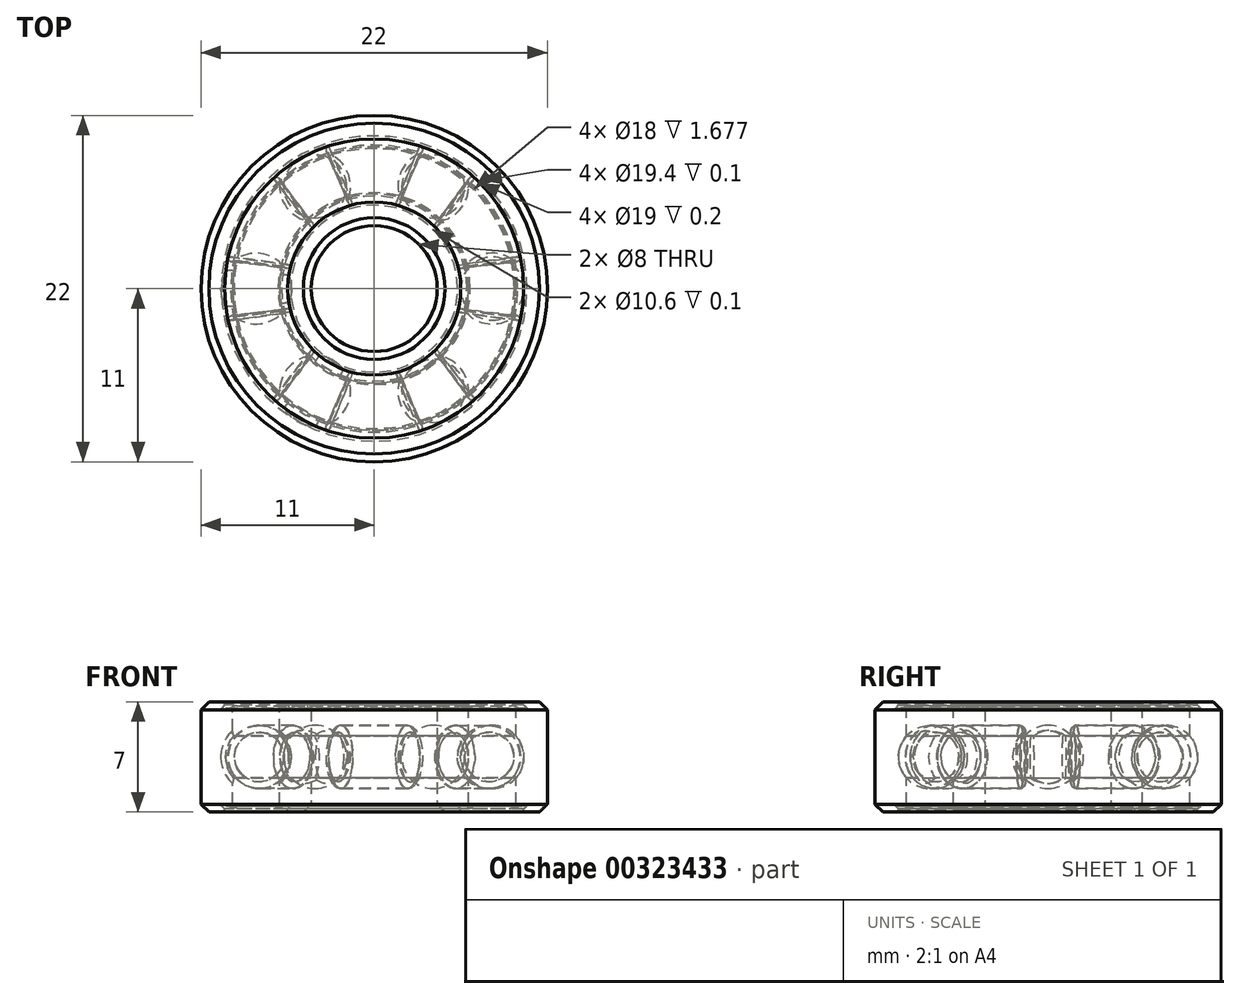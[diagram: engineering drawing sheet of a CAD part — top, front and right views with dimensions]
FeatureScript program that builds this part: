
annotation { "Feature Type Name" : "Feature", "Feature Type Description" : "" }
export const myFeature = defineFeature(function(context is Context, id is Id, definition is map)
    precondition{}
    {
        {
            var Q0;
            Q0=qCreatedBy(makeId("Top.planeOp"),FACE);
            var sketch = newSketch(context, id + "F0", { "sketchPlane" : qUnion([Q0])});
            skCircle(sketch, "E0", {"center": v(0, 0) * mm, "radius": 11 * mm});
            skCircle(sketch, "E1", {"center": v(0, 0) * mm, "radius": 4 * mm});
            skSolve(sketch);
        }
        {
            var Q0;
            Q0=makeQuery(id+"F0.imprint","IMPRINT",FACE,{"disambiguationData":[TD([[makeQuery(id+"F0.imprint","IMPRINT",EDGE,{"derivedFrom":sQuery(id+"F0.wireOp",EDGE,"E0")}),1.0]])]});
            extrude(context, id + "F1", {"entities" : qUnion([Q0]), "depth" : 7 * mm});
        }
        {
            var Q0;
            Q0=makeQuery(id+"F1.opExtrude","CAP_EDGE",EDGE,{"disambiguationData":[OSD([sQuery(id+"F0.wireOp",EDGE,"E0")])],"isStart":false});
            var Q1;
            Q1=makeQuery(id+"F1.opExtrude","CAP_EDGE",EDGE,{"disambiguationData":[OSD([sQuery(id+"F0.wireOp",EDGE,"E0")])],"isStart":true});
            var Q2;
            Q2=makeQuery(id+"F1.opExtrude","SWEPT_FACE",FACE,{"disambiguationData":[OSD([sQuery(id+"F0.wireOp",EDGE,"E1")])]});
            chamfer(context, id + "F2", {"entities" : qUnion([Q0, Q1, Q2]), "width" : .5 * mm, "tangentPropagation" : true});
        }
        {
            var Q0;
            Q0=qCreatedBy(makeId("Front.planeOp"),FACE);
            var sketch = newSketch(context, id + "F3", { "sketchPlane" : qUnion([Q0])});
            skCircle(sketch, "E2", {"center": v(-7.5, 3.5) * mm, "radius": 2 * mm});
            skLineSegment(sketch, "E3.0", {"start": v(-10.5, 7) * mm, "end": v(10.5, 7) * mm, "construction": true});
            skLineSegment(sketch, "E4.0", {"start": v(10.5, 0) * mm, "end": v(-10.5, 0) * mm, "construction": true});
            skLineSegment(sketch, "E5", {"start": v(-7.5, 3.5) * mm, "end": v(-7.5, 7) * mm, "construction": true});
            skLineSegment(sketch, "E6", {"start": v(-7.5, 3.5) * mm, "end": v(-7.5, 0) * mm, "construction": true});
            skLineSegment(sketch, "E7", {"start": v(0, 0) * mm, "end": v(0, 10.43) * mm, "construction": true});
            skLineSegment(sketch, "E8", {"start": v(-4, 0) * mm, "end": v(-4, 7) * mm, "construction": true});
            skLineSegment(sketch, "E9", {"start": v(-11, 0.5) * mm, "end": v(-11, 6.5) * mm});
            skLineSegment(sketch, "E10", {"start": v(-11, 6.5) * mm, "end": v(-10.5, 7) * mm});
            skLineSegment(sketch, "E11", {"start": v(-10.5, 0) * mm, "end": v(-11.25, 0.75) * mm});
            skLineSegment(sketch, "E12", {"start": v(-7.5, 3.5) * mm, "end": v(-11, 3.5) * mm, "construction": true});
            skLineSegment(sketch, "E13", {"start": v(-7.5, 3.5) * mm, "end": v(-4, 3.5) * mm, "construction": true});
            skLineSegment(sketch, "E14", {"start": v(-7.5, 5.5) * mm, "end": v(-7.5, 1.5) * mm});
            skLineSegment(sketch, "E15", {"start": v(-6, 4.82) * mm, "end": v(-6, 7) * mm, "construction": true});
            skLineSegment(sketch, "E16", {"start": v(-6, 7) * mm, "end": v(-9, 7) * mm});
            skLineSegment(sketch, "E17", {"start": v(-9, 7) * mm, "end": v(-9, 4.82) * mm});
            skLineSegment(sketch, "E18", {"start": v(-9, 2.18) * mm, "end": v(-9, 0) * mm});
            skLineSegment(sketch, "E19", {"start": v(-9, 0) * mm, "end": v(-6, 0) * mm});
            skLineSegment(sketch, "E20", {"start": v(-6, 0) * mm, "end": v(-6, 2.18) * mm, "construction": true});
            skLineSegment(sketch, "E21", {"start": v(-6, 6.5) * mm, "end": v(-5.5, 6.5) * mm});
            skLineSegment(sketch, "E22", {"start": v(-5.5, 6.8) * mm, "end": v(-5.5, 7) * mm});
            skLineSegment(sketch, "E23", {"start": v(-6, 0.5) * mm, "end": v(-5.5, 0.5) * mm});
            skLineSegment(sketch, "E24", {"start": v(-5.5, 0.2) * mm, "end": v(-5.5, 0) * mm});
            skLineSegment(sketch, "E25", {"start": v(-6, 2.18) * mm, "end": v(-6, 0.5) * mm});
            skLineSegment(sketch, "E26", {"start": v(-6, 4.82) * mm, "end": v(-6, 6.5) * mm});
            skLineSegment(sketch, "E27", {"start": v(-5.5, 7) * mm, "end": v(-9, 7) * mm});
            skLineSegment(sketch, "E28", {"start": v(-5.5, 0) * mm, "end": v(-9, 0) * mm});
            skLineSegment(sketch, "E29", {"start": v(-5.5, 6.8) * mm, "end": v(-5.3, 6.6) * mm});
            skLineSegment(sketch, "E30", {"start": v(-5.3, 6.6) * mm, "end": v(-5.3, 6.5) * mm});
            skLineSegment(sketch, "E31", {"start": v(-5.3, 6.5) * mm, "end": v(-5.5, 6.5) * mm});
            skLineSegment(sketch, "E32", {"start": v(-5.5, 6.8) * mm, "end": v(-5.5, 6.5) * mm, "construction": true});
            skLineSegment(sketch, "E33.MirrorCS", {"start": v(-9, 6.5) * mm, "end": v(-9.5, 6.5) * mm});
            skLineSegment(sketch, "E34.MirrorCS", {"start": v(-9.7, 6.5) * mm, "end": v(-9.5, 6.5) * mm});
            skLineSegment(sketch, "E35.MirrorCS", {"start": v(-9.7, 6.6) * mm, "end": v(-9.7, 6.5) * mm});
            skLineSegment(sketch, "E36.MirrorCS", {"start": v(-9.5, 6.8) * mm, "end": v(-9.7, 6.6) * mm});
            skLineSegment(sketch, "E37.MirrorCS", {"start": v(-9.5, 6.8) * mm, "end": v(-9.5, 7) * mm});
            skLineSegment(sketch, "E38", {"start": v(-9.5, 7) * mm, "end": v(-9, 7) * mm});
            skLineSegment(sketch, "E39.MirrorCS", {"start": v(-5.3, 0.5) * mm, "end": v(-5.5, 0.5) * mm});
            skLineSegment(sketch, "E40.MirrorCS", {"start": v(-5.3, 0.4) * mm, "end": v(-5.3, 0.5) * mm});
            skLineSegment(sketch, "E41.MirrorCS", {"start": v(-5.5, 0.2) * mm, "end": v(-5.3, 0.4) * mm});
            skLineSegment(sketch, "E42.MirrorCS", {"start": v(-9, 0.5) * mm, "end": v(-9.5, 0.5) * mm});
            skLineSegment(sketch, "E43.MirrorCS", {"start": v(-9.7, 0.5) * mm, "end": v(-9.5, 0.5) * mm});
            skLineSegment(sketch, "E44.MirrorCS", {"start": v(-9.5, 0.2) * mm, "end": v(-9.7, 0.4) * mm});
            skLineSegment(sketch, "E45.MirrorCS", {"start": v(-9.5, 0.2) * mm, "end": v(-9.5, 0) * mm});
            skLineSegment(sketch, "E46.MirrorCS", {"start": v(-9.7, 0.4) * mm, "end": v(-9.7, 0.5) * mm});
            skLineSegment(sketch, "E47", {"start": v(-5.5, 0.2) * mm, "end": v(-5.5, 0.5) * mm, "construction": true});
            skLineSegment(sketch, "E48", {"start": v(-9, 0) * mm, "end": v(-9.5, 0) * mm});
            skSolve(sketch);
        }
        {
            var Q0;
            Q0 = qSketchRegion(id + "F3", true);
            var Q1;
            Q1=sQuery(id+"F3.wireOp",EDGE,"E7");
            revolve(context, id + "F4", {"operationType" : NewBodyOperationType.REMOVE, "entities" : qUnion([Q0]), "axis" : qUnion([Q1]), "revolveType" : RevolveType.FULL, "oppositeDirection" : true});
        }
        {
            var Q0;
            {var subQ0=sQuery(id+"F3.wireOp",EDGE,"E14");Q0=makeQuery(id+"F3.imprint","IMPRINT",FACE,{"disambiguationData":[TD([[makeQuery(id+"F3.imprint","IMPRINT",EDGE,{"derivedFrom":subQ0}),1.0]])]});}
            var Q1;
            Q1=sQuery(id+"F3.wireOp",EDGE,"E14");
            revolve(context, id + "F5", {"entities" : qUnion([Q0]), "axis" : qUnion([Q1]), "revolveType" : RevolveType.FULL});
        }
        {
            var Q0;
            Q0=makeQuery(id+"F5.opRevolve","SWEPT_BODY",BODY,{"disambiguationData":[OSD([sQuery(id+"F3.wireOp",EDGE,"E2"),sQuery(id+"F3.wireOp",EDGE,"E14")])]});
            var Q1;
            Q1=makeQuery(id+"F1.opExtrude","SWEPT_FACE",FACE,{"disambiguationData":[OSD([sQuery(id+"F0.wireOp",EDGE,"E1")])]});
            circularPattern(context, id + "F6", {"entities" : qUnion([Q0]), "axis" : qUnion([Q1]), "angle" : 360 * degree, "instanceCount" : 6, "equalSpace" : true});
        }
        {
            var Q0;
            {var subQ0=sQuery(id+"F3.wireOp",EDGE,"E14");Q0=makeQuery(id+"F3.imprint","IMPRINT",FACE,{"disambiguationData":[TD([[makeQuery(id+"F3.imprint","IMPRINT",EDGE,{"derivedFrom":subQ0}),1.0]])]});}
            var Q1;
            {var subQ0=sQuery(id+"F3.wireOp",EDGE,"E14");Q1=makeQuery(id+"F3.imprint","IMPRINT",FACE,{"disambiguationData":[TD([[makeQuery(id+"F3.imprint","IMPRINT",EDGE,{"derivedFrom":subQ0}),-1.0]])]});}
            var Q2;
            Q2=sQuery(id+"F3.wireOp",EDGE,"E7");
            revolve(context, id + "F7", {"entities" : qUnion([Q0, Q1]), "axis" : qUnion([Q2]), "revolveType" : RevolveType.ONE_DIRECTION, "angle" : 60 * degree});
        }
        {
            var Q0;
            {var subQ0=sQuery(id+"F0.wireOp",EDGE,"E1");Q0=makeQuery(id+"F4.boolean.opBoolean","SPLIT",FACE,{"disambiguationData":[TD([makeQuery(id+"F4.opRevolve","SWEPT_FACE",FACE,{"disambiguationData":[OSD([sQuery(id+"F3.wireOp",EDGE,"E22")])]})])],"derivedFrom":makeQuery(id+"F1.opExtrude","CAP_FACE",FACE,{"disambiguationData":[OSD([sQuery(id+"F0.wireOp",EDGE,"E0"),subQ0])],"isStart":false})});}
            var Q1;
            {var subQ0=sQuery(id+"F0.wireOp",EDGE,"E1");Q1=makeQuery(id+"F4.boolean.opBoolean","SPLIT",FACE,{"disambiguationData":[TD([makeQuery(id+"F4.opRevolve","SWEPT_FACE",FACE,{"disambiguationData":[OSD([sQuery(id+"F3.wireOp",EDGE,"E24")])]})])],"derivedFrom":makeQuery(id+"F1.opExtrude","CAP_FACE",FACE,{"disambiguationData":[OSD([sQuery(id+"F0.wireOp",EDGE,"E0"),subQ0])],"isStart":true})});}
            cPlane(context, id + "F8", {"entities" : qUnion([Q0, Q1]), "cplaneType" : CPlaneType.MID_PLANE, "offset" : 25 * mm, "width" : 150 * mm, "height" : 150 * mm});
        }
        {
            var Q0;
            Q0=qCreatedBy(id+"F8.planeOp",FACE);
            var sketch = newSketch(context, id + "F9", { "sketchPlane" : qUnion([Q0])});
            skCircle(sketch, "E49", {"center": v(-7.5, 0) * mm, "radius": 2 * mm, "construction": true});
            skArc(sketch, "E50", {"start": v(-5.25, 0) * mm, "mid": v(-7.5, 2.25) * mm, "end": v(-9.75, 0) * mm});
            skLineSegment(sketch, "E51", {"start": v(-5.25, 0) * mm, "end": v(-9.75, 0) * mm});
            skCircle(sketch, "E52", {"center": v(-3.75, -6.5) * mm, "radius": 2 * mm, "construction": true});
            skArc(sketch, "E53", {"start": v(-4.88, -8.44) * mm, "mid": v(-1.8, -7.62) * mm, "end": v(-2.63, -4.55) * mm});
            skLineSegment(sketch, "E54", {"start": v(-2.63, -4.55) * mm, "end": v(-4.88, -8.44) * mm});
            skLineSegment(sketch, "E55", {"start": v(0, 0) * mm, "end": v(-2.63, -4.55) * mm, "construction": true});
            skLineSegment(sketch, "E56", {"start": v(0, 0) * mm, "end": v(-5.25, 0) * mm, "construction": true});
            skSolve(sketch);
        }
        {
            var Q0;
            Q0=makeQuery(id+"F9.imprint","IMPRINT",FACE,{"disambiguationData":[TD([[makeQuery(id+"F9.imprint","IMPRINT",EDGE,{"derivedFrom":sQuery(id+"F9.wireOp",EDGE,"E50")}),1.0]])]});
            var Q1;
            Q1=sQuery(id+"F9.wireOp",EDGE,"E51");
            revolve(context, id + "F10", {"operationType" : NewBodyOperationType.REMOVE, "entities" : qUnion([Q0]), "axis" : qUnion([Q1]), "revolveType" : RevolveType.FULL, "oppositeDirection" : true});
        }
        {
            var Q0;
            Q0=makeQuery(id+"F9.imprint","IMPRINT",FACE,{"disambiguationData":[TD([[makeQuery(id+"F9.imprint","IMPRINT",EDGE,{"derivedFrom":sQuery(id+"F9.wireOp",EDGE,"E53")}),1.0]])]});
            var Q1;
            Q1=sQuery(id+"F9.wireOp",EDGE,"E54");
            revolve(context, id + "F11", {"operationType" : NewBodyOperationType.REMOVE, "entities" : qUnion([Q0]), "axis" : qUnion([Q1]), "revolveType" : RevolveType.FULL, "oppositeDirection" : true});
        }
        {
            var Q0;
            Q0=makeQuery(id+"F11.boolean.opBoolean","INTERSECT",EDGE,{"derivedFrom":[makeQuery(id+"F7.opRevolve","SWEPT_FACE",FACE,{"disambiguationData":[OSD([sQuery(id+"F3.wireOp",EDGE,"E2")])]}),makeQuery(id+"F11.opRevolve","SWEPT_FACE",FACE,{"disambiguationData":[OSD([sQuery(id+"F9.wireOp",EDGE,"E53")])]})]});
            var Q1;
            Q1=makeQuery(id+"F10.boolean.opBoolean","INTERSECT",EDGE,{"derivedFrom":[makeQuery(id+"F7.opRevolve","SWEPT_FACE",FACE,{"disambiguationData":[OSD([sQuery(id+"F3.wireOp",EDGE,"E2")])]}),makeQuery(id+"F10.opRevolve","SWEPT_FACE",FACE,{"disambiguationData":[OSD([sQuery(id+"F9.wireOp",EDGE,"E50")])]})]});
            fillet(context, id + "F12", {"entities" : qUnion([Q0, Q1]), "radius" : .25 * mm, "tangentPropagation" : true, "allowEdgeOverflow" : false});
        }
        {
            var Q0;
            Q0=makeQuery(id+"F7.opRevolve","SWEPT_BODY",BODY,{"disambiguationData":[OSD([sQuery(id+"F3.wireOp",EDGE,"E2")])]});
            var Q1;
            Q1=makeQuery(id+"F1.opExtrude","SWEPT_FACE",FACE,{"disambiguationData":[OSD([sQuery(id+"F0.wireOp",EDGE,"E1")])]});
            circularPattern(context, id + "F13", {"entities" : qUnion([Q0]), "axis" : qUnion([Q1]), "angle" : 360 * degree, "instanceCount" : 6, "equalSpace" : true});
        }
        {
            var Q0;
            Q0=qCreatedBy(makeId("Front.planeOp"),FACE);
            var sketch = newSketch(context, id + "F14", { "sketchPlane" : qUnion([Q0])});
            skPoint(sketch, "E57.0", {"position": v(-5.3, 6.5) * mm});
            skPoint(sketch, "E58.0", {"position": v(-5.3, 6.6) * mm});
            skPoint(sketch, "E59.0", {"position": v(-9.7, 6.5) * mm});
            skPoint(sketch, "E60.0", {"position": v(-9.7, 6.6) * mm});
            skLineSegment(sketch, "E61", {"start": v(-9.7, 6.5) * mm, "end": v(-9.12, 6.5) * mm});
            skLineSegment(sketch, "E62", {"start": v(-9.12, 6.5) * mm, "end": v(-8.9, 6.6) * mm});
            skLineSegment(sketch, "E63", {"start": v(-8.9, 6.6) * mm, "end": v(-6.1, 6.6) * mm});
            skLineSegment(sketch, "E64", {"start": v(-6.1, 6.6) * mm, "end": v(-5.88, 6.5) * mm});
            skLineSegment(sketch, "E65", {"start": v(-5.88, 6.5) * mm, "end": v(-5.3, 6.5) * mm});
            skLineSegment(sketch, "E66", {"start": v(-5.3, 6.6) * mm, "end": v(-5.8, 6.6) * mm});
            skLineSegment(sketch, "E67", {"start": v(-5.8, 6.6) * mm, "end": v(-6.12, 6.75) * mm});
            skLineSegment(sketch, "E68", {"start": v(-6.12, 6.75) * mm, "end": v(-8.88, 6.75) * mm});
            skLineSegment(sketch, "E69", {"start": v(-8.88, 6.75) * mm, "end": v(-9.2, 6.6) * mm});
            skLineSegment(sketch, "E70", {"start": v(-9.2, 6.6) * mm, "end": v(-9.7, 6.6) * mm});
            skLineSegment(sketch, "E71", {"start": v(-5.3, 6.6) * mm, "end": v(-5.3, 6.5) * mm});
            skLineSegment(sketch, "E72", {"start": v(-9.7, 6.6) * mm, "end": v(-9.7, 6.5) * mm});
            skSolve(sketch);
        }
        {
            var Q0;
            Q0=makeQuery(id+"F14.imprint","IMPRINT",FACE,{"disambiguationData":[TD([[makeQuery(id+"F14.imprint","IMPRINT",EDGE,{"derivedFrom":sQuery(id+"F14.wireOp",EDGE,"E61")}),1.0]])]});
            var Q1;
            Q1=makeQuery(id+"F1.opExtrude","SWEPT_FACE",FACE,{"disambiguationData":[OSD([sQuery(id+"F0.wireOp",EDGE,"E1")])]});
            revolve(context, id + "F15", {"surfaceOperationType" : NewSurfaceOperationType.NEW, "entities" : qUnion([Q0]), "axis" : qUnion([Q1]), "revolveType" : RevolveType.FULL});
        }
        {
            var Q0;
            Q0=makeQuery(id+"F15.opRevolve","SWEPT_EDGE",EDGE,{"disambiguationData":[OSD([sQuery(id+"F14.wireOp",EDGE,"E66"),sQuery(id+"F14.wireOp",EDGE,"E67")])]});
            var Q1;
            Q1=makeQuery(id+"F15.opRevolve","SWEPT_EDGE",EDGE,{"disambiguationData":[OSD([sQuery(id+"F14.wireOp",EDGE,"E69"),sQuery(id+"F14.wireOp",EDGE,"E70")])]});
            var Q2;
            Q2=makeQuery(id+"F15.opRevolve","SWEPT_EDGE",EDGE,{"disambiguationData":[OSD([sQuery(id+"F14.wireOp",EDGE,"E67"),sQuery(id+"F14.wireOp",EDGE,"E68")])]});
            var Q3;
            Q3=makeQuery(id+"F15.opRevolve","SWEPT_EDGE",EDGE,{"disambiguationData":[OSD([sQuery(id+"F14.wireOp",EDGE,"E68"),sQuery(id+"F14.wireOp",EDGE,"E69")])]});
            fillet(context, id + "F16", {"entities" : qUnion([Q0, Q1, Q2, Q3]), "radius" : .8 * mm, "tangentPropagation" : true, "allowEdgeOverflow" : false});
        }
        {
            var Q0;
            Q0=makeQuery(id+"F15.opRevolve","SWEPT_BODY",BODY,{"disambiguationData":[OSD([sQuery(id+"F14.wireOp",EDGE,"E61"),sQuery(id+"F14.wireOp",EDGE,"E62"),sQuery(id+"F14.wireOp",EDGE,"E63"),sQuery(id+"F14.wireOp",EDGE,"E64"),sQuery(id+"F14.wireOp",EDGE,"E65"),sQuery(id+"F14.wireOp",EDGE,"E66"),sQuery(id+"F14.wireOp",EDGE,"E67"),sQuery(id+"F14.wireOp",EDGE,"E68"),sQuery(id+"F14.wireOp",EDGE,"E69"),sQuery(id+"F14.wireOp",EDGE,"E70"),sQuery(id+"F14.wireOp",EDGE,"E71"),sQuery(id+"F14.wireOp",EDGE,"E72")])]});
            var Q1;
            Q1=qCreatedBy(id+"F8.planeOp",FACE);
            mirror(context, id + "F17", {"entities" : qUnion([Q0]), "mirrorPlane" : qUnion([Q1])});
        }
    });
